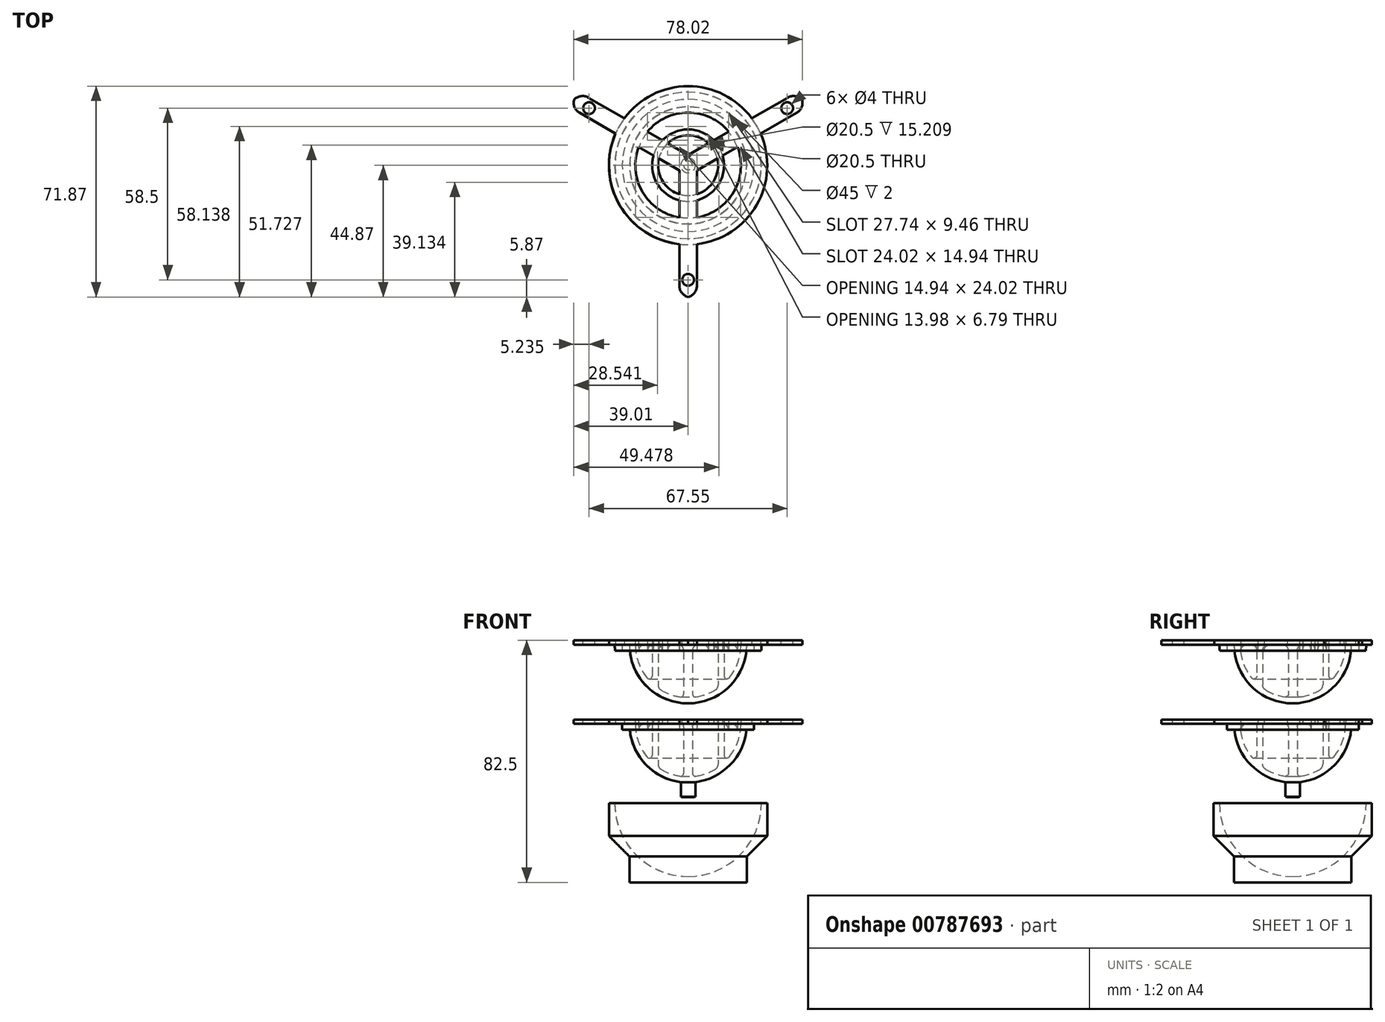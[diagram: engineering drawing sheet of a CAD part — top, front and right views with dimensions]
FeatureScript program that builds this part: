
annotation { "Feature Type Name" : "Feature", "Feature Type Description" : "" }
export const myFeature = defineFeature(function(context is Context, id is Id, definition is map)
    precondition{}
    {
        {
            var Q0;
            Q0=qCreatedBy(makeId("Front.planeOp"),FACE);
            var sketch = newSketch(context, id + "F0", { "sketchPlane" : qUnion([Q0])});
            skLineSegment(sketch, "E0.bottom", {"start": v(0, 0) * mm, "end": v(-27, 0) * mm});
            skLineSegment(sketch, "E0.top", {"start": v(0, 27) * mm, "end": v(-27, 27) * mm});
            skLineSegment(sketch, "E0.left", {"start": v(0, 0) * mm, "end": v(0, 27) * mm});
            skLineSegment(sketch, "E0.right", {"start": v(-27, 0) * mm, "end": v(-27, 27) * mm});
            skArc(sketch, "E1", {"start": v(-25, 27) * mm, "mid": v(-17.68, 9.32) * mm, "end": v(0, 2) * mm});
            skLineSegment(sketch, "E2", {"start": v(-25, 27) * mm, "end": v(-25, 19.7) * mm, "construction": true});
            skLineSegment(sketch, "E3", {"start": v(0, 2) * mm, "end": v(-8.55, 2) * mm, "construction": true});
            skArc(sketch, "E4", {"start": v(-20, 27) * mm, "mid": v(-14.14, 12.86) * mm, "end": v(0, 7) * mm});
            skLineSegment(sketch, "E5", {"start": v(-20, 27) * mm, "end": v(-20, 19.7) * mm, "construction": true});
            skLineSegment(sketch, "E6", {"start": v(0, 7) * mm, "end": v(-8.55, 7) * mm, "construction": true});
            skLineSegment(sketch, "E7", {"start": v(-27, 15.82) * mm, "end": v(-11.18, 0) * mm});
            skPoint(sketch, "E8", {"position": v(-13.5, 0) * mm});
            skLineSegment(sketch, "E9.bottom", {"start": v(0, 27) * mm, "end": v(-22.5, 27) * mm});
            skLineSegment(sketch, "E9.top", {"start": v(0, 25) * mm, "end": v(-22.5, 25) * mm});
            skLineSegment(sketch, "E9.left", {"start": v(0, 27) * mm, "end": v(0, 25) * mm});
            skLineSegment(sketch, "E9.right", {"start": v(-22.5, 27) * mm, "end": v(-22.5, 25) * mm});
            skLineSegment(sketch, "E10", {"start": v(-30, 0) * mm, "end": v(-30, 18.82) * mm});
            skLineSegment(sketch, "E11.top", {"start": v(0, 28.5) * mm, "end": v(-27, 28.5) * mm});
            skLineSegment(sketch, "E11.left", {"start": v(0, 27) * mm, "end": v(0, 28.5) * mm});
            skLineSegment(sketch, "E11.right", {"start": v(-27, 27) * mm, "end": v(-27, 28.5) * mm});
            skLineSegment(sketch, "E12.bottom", {"start": v(-3, 28.5) * mm, "end": v(3, 28.5) * mm});
            skLineSegment(sketch, "E12.top", {"start": v(-3, 27) * mm, "end": v(3, 27) * mm});
            skLineSegment(sketch, "E12.left", {"start": v(-3, 28.5) * mm, "end": v(-3, 27) * mm});
            skLineSegment(sketch, "E12.right", {"start": v(3, 28.5) * mm, "end": v(3, 27) * mm});
            skArc(sketch, "E13", {"start": v(-18, 27) * mm, "mid": v(-16.98, 21.02) * mm, "end": v(-14.03, 15.72) * mm, "construction": true});
            skLineSegment(sketch, "E14.bottom", {"start": v(0, 25) * mm, "end": v(-1.5, 25) * mm});
            skLineSegment(sketch, "E14.left", {"start": v(0, 25) * mm, "end": v(0, 7) * mm});
            skLineSegment(sketch, "E14.right", {"start": v(-1.5, 25) * mm, "end": v(-1.5, 10.18) * mm});
            skArc(sketch, "E15.filletArc", {"start": v(-2.65, 9.2) * mm, "mid": v(-1.85, 9.43) * mm, "end": v(-1.5, 10.18) * mm});
            skLineSegment(sketch, "E16", {"start": v(-11.25, 25) * mm, "end": v(-11.25, 12.95) * mm, "construction": true});
            skLineSegment(sketch, "E17", {"start": v(-12.25, 25) * mm, "end": v(-12.25, 16.35) * mm});
            skLineSegment(sketch, "E18", {"start": v(-10.25, 25) * mm, "end": v(-10.25, 13.3) * mm});
            skArc(sketch, "E19", {"start": v(-18, 27) * mm, "mid": v(-16.98, 21.02) * mm, "end": v(-14.03, 15.72) * mm});
            skArc(sketch, "E20", {"start": v(-9.28, 11.58) * mm, "mid": v(-6.08, 10.06) * mm, "end": v(-2.65, 9.2) * mm});
            skArc(sketch, "E21.filletArc", {"start": v(-14.03, 15.72) * mm, "mid": v(-12.92, 15.4) * mm, "end": v(-12.25, 16.35) * mm});
            skPoint(sketch, "E22.visualSharp", {"position": v(-10.25, 12.2) * mm});
            skArc(sketch, "E22.filletArc", {"start": v(-10.25, 13.3) * mm, "mid": v(-10, 12.3) * mm, "end": v(-9.28, 11.58) * mm});
            skLineSegment(sketch, "E23", {"start": v(-12.25, 25) * mm, "end": v(-12.25, 28.5) * mm});
            skLineSegment(sketch, "E24", {"start": v(-10.25, 25) * mm, "end": v(-10.25, 28.5) * mm});
            skLineSegment(sketch, "E25", {"start": v(-18, 27) * mm, "end": v(-18, 28.5) * mm});
            skLineSegment(sketch, "E26", {"start": v(-1.5, 25) * mm, "end": v(-1.5, 27) * mm});
            skLineSegment(sketch, "E27", {"start": v(-2.5, 7.16) * mm, "end": v(-2.5, 2.13) * mm});
            skLineSegment(sketch, "E28", {"start": v(-22.5, 25) * mm, "end": v(-24.92, 25) * mm});
            skLineSegment(sketch, "E29", {"start": v(-20, 0) * mm, "end": v(-20, 8.82) * mm});
            skSolve(sketch);
        }
        {
            var Q0;
            {var subQ0=sQuery(id+"F0.wireOp",EDGE,"E0.left");var subQ1=sQuery(id+"F0.wireOp",EDGE,"E0.bottom");var subQ2=makeQuery(id+"F0.imprint","INTERSECT",VERTEX,{"derivedFrom":[subQ1,subQ0]});Q0=makeQuery(id+"F0.imprint","IMPRINT",FACE,{"disambiguationData":[TD([[makeQuery(id+"F0.imprint","IMPRINT",EDGE,{"disambiguationData":[TD([[subQ2,-1.0]])],"derivedFrom":subQ1}),-1.0]])]});}
            var Q1;
            {var subQ3=sQuery(id+"F0.wireOp",EDGE,"E10");Q1=makeQuery(id+"F0.imprint","IMPRINT",FACE,{"disambiguationData":[TD([[makeQuery(id+"F0.imprint","IMPRINT",EDGE,{"derivedFrom":subQ3}),-1.0]])]});}
            var Q2;
            {var subQ0=sQuery(id+"F0.wireOp",EDGE,"E29");Q2=makeQuery(id+"F0.imprint","IMPRINT",FACE,{"disambiguationData":[TD([[makeQuery(id+"F0.imprint","IMPRINT",EDGE,{"derivedFrom":subQ0}),-1.0]])]});}
            var Q3;
            Q3=sQuery(id+"F0.wireOp",EDGE,"E0.left");
            revolve(context, id + "F1", {"surfaceOperationType" : NewSurfaceOperationType.NEW, "entities" : qUnion([Q0, Q1, Q2]), "axis" : qUnion([Q3]), "revolveType" : RevolveType.FULL});
        }
        {
            var Q0;
            {var subQ6=sQuery(id+"F0.wireOp",EDGE,"E14.right");Q0=makeQuery(id+"F0.imprint","IMPRINT",FACE,{"disambiguationData":[TD([[makeQuery(id+"F0.imprint","IMPRINT",EDGE,{"derivedFrom":subQ6}),1.0]])]});}
            var Q1;
            {var subQ5=sQuery(id+"F0.wireOp",EDGE,"E27");Q1=makeQuery(id+"F0.imprint","IMPRINT",FACE,{"disambiguationData":[TD([[makeQuery(id+"F0.imprint","IMPRINT",EDGE,{"derivedFrom":subQ5}),1.0]])]});}
            var Q2;
            {var subQ0=sQuery(id+"F0.wireOp",EDGE,"E26");Q2=makeQuery(id+"F0.imprint","IMPRINT",FACE,{"disambiguationData":[TD([[makeQuery(id+"F0.imprint","IMPRINT",EDGE,{"derivedFrom":subQ0}),-1.0]])]});}
            var Q3;
            {var subQ0=sQuery(id+"F0.wireOp",EDGE,"E11.left");Q3=makeQuery(id+"F0.imprint","IMPRINT",FACE,{"disambiguationData":[TD([[makeQuery(id+"F0.imprint","IMPRINT",EDGE,{"derivedFrom":subQ0}),1.0]])]});}
            var Q4;
            {var subQ0=sQuery(id+"F0.wireOp",EDGE,"E24");var subQ1=sQuery(id+"F0.wireOp",EDGE,"E0.top");var subQ2=makeQuery(id+"F0.imprint","INTERSECT",VERTEX,{"derivedFrom":[subQ1,subQ0]});Q4=makeQuery(id+"F0.imprint","IMPRINT",FACE,{"disambiguationData":[TD([[makeQuery(id+"F0.imprint","IMPRINT",EDGE,{"disambiguationData":[TD([[subQ2,-1.0]])],"derivedFrom":subQ1}),1.0]])]});}
            var Q5;
            {var subQ0=sQuery(id+"F0.wireOp",EDGE,"E24");var subQ1=sQuery(id+"F0.wireOp",EDGE,"E0.top");var subQ2=makeQuery(id+"F0.imprint","INTERSECT",VERTEX,{"derivedFrom":[subQ1,subQ0]});Q5=makeQuery(id+"F0.imprint","IMPRINT",FACE,{"disambiguationData":[TD([[makeQuery(id+"F0.imprint","IMPRINT",EDGE,{"disambiguationData":[TD([[subQ2,-1.0]])],"derivedFrom":subQ1}),-1.0]])]});}
            var Q6;
            {var subQ0=sQuery(id+"F0.wireOp",EDGE,"E4");var subQ1=sQuery(id+"F0.wireOp",EDGE,"E0.top");var subQ2=makeQuery(id+"F0.imprint","INTERSECT",VERTEX,{"derivedFrom":[subQ1,subQ0]});Q6=makeQuery(id+"F0.imprint","IMPRINT",FACE,{"disambiguationData":[TD([[makeQuery(id+"F0.imprint","IMPRINT",EDGE,{"disambiguationData":[TD([[subQ2,-1.0]])],"derivedFrom":subQ0}),1.0]])]});}
            var Q7;
            {var subQ3=sQuery(id+"F0.wireOp",EDGE,"E9.right");Q7=makeQuery(id+"F0.imprint","IMPRINT",FACE,{"disambiguationData":[TD([[makeQuery(id+"F0.imprint","IMPRINT",EDGE,{"derivedFrom":subQ3}),1.0]])]});}
            var Q8;
            {var subQ3=sQuery(id+"F0.wireOp",EDGE,"E11.right");Q8=makeQuery(id+"F0.imprint","IMPRINT",FACE,{"disambiguationData":[TD([[makeQuery(id+"F0.imprint","IMPRINT",EDGE,{"derivedFrom":subQ3}),-1.0]])]});}
            var Q9;
            Q9=sQuery(id+"F0.wireOp",EDGE,"E0.left");
            revolve(context, id + "F2", {"surfaceOperationType" : NewSurfaceOperationType.NEW, "entities" : qUnion([Q0, Q1, Q2, Q3, Q4, Q5, Q6, Q7, Q8]), "axis" : qUnion([Q9]), "revolveType" : RevolveType.FULL});
        }
        {
            var Q0;
            {var subQ6=sQuery(id+"F0.wireOp",EDGE,"E14.right");Q0=makeQuery(id+"F0.imprint","IMPRINT",FACE,{"disambiguationData":[TD([[makeQuery(id+"F0.imprint","IMPRINT",EDGE,{"derivedFrom":subQ6}),1.0]])]});}
            var Q1;
            {var subQ0=sQuery(id+"F0.wireOp",EDGE,"E26");Q1=makeQuery(id+"F0.imprint","IMPRINT",FACE,{"disambiguationData":[TD([[makeQuery(id+"F0.imprint","IMPRINT",EDGE,{"derivedFrom":subQ0}),-1.0]])]});}
            var Q2;
            {var subQ0=sQuery(id+"F0.wireOp",EDGE,"E11.left");Q2=makeQuery(id+"F0.imprint","IMPRINT",FACE,{"disambiguationData":[TD([[makeQuery(id+"F0.imprint","IMPRINT",EDGE,{"derivedFrom":subQ0}),1.0]])]});}
            var Q3;
            {var subQ0=sQuery(id+"F0.wireOp",EDGE,"E24");var subQ1=sQuery(id+"F0.wireOp",EDGE,"E0.top");var subQ2=makeQuery(id+"F0.imprint","INTERSECT",VERTEX,{"derivedFrom":[subQ1,subQ0]});Q3=makeQuery(id+"F0.imprint","IMPRINT",FACE,{"disambiguationData":[TD([[makeQuery(id+"F0.imprint","IMPRINT",EDGE,{"disambiguationData":[TD([[subQ2,-1.0]])],"derivedFrom":subQ1}),1.0]])]});}
            var Q4;
            {var subQ0=sQuery(id+"F0.wireOp",EDGE,"E24");var subQ1=sQuery(id+"F0.wireOp",EDGE,"E0.top");var subQ2=makeQuery(id+"F0.imprint","INTERSECT",VERTEX,{"derivedFrom":[subQ1,subQ0]});Q4=makeQuery(id+"F0.imprint","IMPRINT",FACE,{"disambiguationData":[TD([[makeQuery(id+"F0.imprint","IMPRINT",EDGE,{"disambiguationData":[TD([[subQ2,-1.0]])],"derivedFrom":subQ1}),-1.0]])]});}
            var Q5;
            {var subQ0=sQuery(id+"F0.wireOp",EDGE,"E4");var subQ1=sQuery(id+"F0.wireOp",EDGE,"E0.top");var subQ2=makeQuery(id+"F0.imprint","INTERSECT",VERTEX,{"derivedFrom":[subQ1,subQ0]});Q5=makeQuery(id+"F0.imprint","IMPRINT",FACE,{"disambiguationData":[TD([[makeQuery(id+"F0.imprint","IMPRINT",EDGE,{"disambiguationData":[TD([[subQ2,-1.0]])],"derivedFrom":subQ0}),1.0]])]});}
            var Q6;
            {var subQ3=sQuery(id+"F0.wireOp",EDGE,"E11.right");Q6=makeQuery(id+"F0.imprint","IMPRINT",FACE,{"disambiguationData":[TD([[makeQuery(id+"F0.imprint","IMPRINT",EDGE,{"derivedFrom":subQ3}),-1.0]])]});}
            var Q7;
            {var subQ3=sQuery(id+"F0.wireOp",EDGE,"E9.right");Q7=makeQuery(id+"F0.imprint","IMPRINT",FACE,{"disambiguationData":[TD([[makeQuery(id+"F0.imprint","IMPRINT",EDGE,{"derivedFrom":subQ3}),-1.0]])]});}
            var Q8;
            Q8=sQuery(id+"F0.wireOp",EDGE,"E0.left");
            revolve(context, id + "F3", {"surfaceOperationType" : NewSurfaceOperationType.NEW, "entities" : qUnion([Q0, Q1, Q2, Q3, Q4, Q5, Q6, Q7]), "axis" : qUnion([Q8]), "revolveType" : RevolveType.FULL});
        }
        {
            var Q0;
            Q0=makeQuery(id+"F2.opRevolve","SWEPT_EDGE",EDGE,{"disambiguationData":[OSD([sQuery(id+"F0.wireOp",EDGE,"E0.top"),sQuery(id+"F0.wireOp",EDGE,"E26")])]});
            fillet(context, id + "F4", {"entities" : qUnion([Q0]), "radius" : 1 * mm, "tangentPropagation" : true, "allowEdgeOverflow" : false});
        }
        {
            var Q0;
            Q0=makeQuery(id+"F0.imprint","IMPRINT",FACE,{"disambiguationData":[TD([[makeQuery(id+"F0.imprint","IMPRINT",EDGE,{"derivedFrom":sQuery(id+"F0.wireOp",EDGE,"E11.left")}),-1.0]])]});
            var Q1;
            {var subQ0=sQuery(id+"F0.wireOp",EDGE,"E11.left");Q1=makeQuery(id+"F0.imprint","IMPRINT",FACE,{"disambiguationData":[TD([[makeQuery(id+"F0.imprint","IMPRINT",EDGE,{"derivedFrom":subQ0}),1.0]])]});}
            extrude(context, id + "F5", {"entities" : qUnion([Q0, Q1]), "depth" : 45 * mm, "offsetDistance" : 25 * mm});
        }
        {
            var Q0;
            Q0=makeQuery(id+"F5.opExtrude","SWEPT_FACE",FACE,{"disambiguationData":[OSD([sQuery(id+"F0.wireOp",EDGE,"E11.top"),sQuery(id+"F0.wireOp",EDGE,"E12.bottom")])]});
            var sketch = newSketch(context, id + "F6", { "sketchPlane" : qUnion([Q0])});
            skLineSegment(sketch, "E30.0", {"start": v(-3, -45) * mm, "end": v(-3, 0) * mm});
            skLineSegment(sketch, "E30.1", {"start": v(-3, -45) * mm, "end": v(3, -45) * mm});
            skLineSegment(sketch, "E30.2", {"start": v(3, -45) * mm, "end": v(3, 0) * mm});
            skLineSegment(sketch, "E31", {"start": v(0, -65.08) * mm, "end": v(0, -45) * mm, "construction": true});
            skLineSegment(sketch, "E32", {"start": v(3, -39) * mm, "end": v(-3, -39) * mm, "construction": true});
            skCircle(sketch, "E33", {"center": v(0, -39) * mm, "radius": 2 * mm});
            skSolve(sketch);
        }
        {
            var Q0;
            Q0=makeQuery(id+"F6.imprint","IMPRINT",FACE,{"disambiguationData":[TD([[makeQuery(id+"F6.imprint","IMPRINT",EDGE,{"derivedFrom":sQuery(id+"F6.wireOp",EDGE,"E33")}),1.0]])]});
            extrude(context, id + "F7", {"entities" : qUnion([Q0]), "operationType" : NewBodyOperationType.REMOVE, "endBound" : BoundingType.UP_TO_NEXT, "oppositeDirection" : true, "depth" : 25 * mm, "offsetDistance" : 25 * mm});
        }
        {
            var Q0;
            Q0=makeQuery(id+"F5.opExtrude","CAP_EDGE",EDGE,{"disambiguationData":[OSD([sQuery(id+"F0.wireOp",EDGE,"E12.right")])],"isStart":false});
            var Q1;
            Q1=makeQuery(id+"F5.opExtrude","CAP_EDGE",EDGE,{"disambiguationData":[OSD([sQuery(id+"F0.wireOp",EDGE,"E12.left")])],"isStart":false});
            fillet(context, id + "F8", {"entities" : qUnion([Q0, Q1]), "radius" : 4 * mm, "tangentPropagation" : true, "allowEdgeOverflow" : false});
        }
        {
            var Q0;
            Q0=makeQuery(id+"F5.opExtrude","SWEPT_BODY",BODY,{"disambiguationData":[OSD([sQuery(id+"F0.wireOp",EDGE,"E0.top"),sQuery(id+"F0.wireOp",EDGE,"E11.top"),sQuery(id+"F0.wireOp",EDGE,"E12.bottom"),sQuery(id+"F0.wireOp",EDGE,"E12.top"),sQuery(id+"F0.wireOp",EDGE,"E12.left"),sQuery(id+"F0.wireOp",EDGE,"E12.right")])]});
            var Q1;
            Q1=sQuery(id+"F0.wireOp",EDGE,"E0.left");
            circularPattern(context, id + "F9", {"entities" : qUnion([Q0]), "axis" : qUnion([Q1]), "angle" : 360 * degree, "instanceCount" : 3, "equalSpace" : true});
        }
        {
            var Q0;
            Q0=makeQuery(id+"F5.opExtrude","SWEPT_BODY",BODY,{"disambiguationData":[OSD([sQuery(id+"F0.wireOp",EDGE,"E0.top"),sQuery(id+"F0.wireOp",EDGE,"E11.top"),sQuery(id+"F0.wireOp",EDGE,"E12.bottom"),sQuery(id+"F0.wireOp",EDGE,"E12.top"),sQuery(id+"F0.wireOp",EDGE,"E12.left"),sQuery(id+"F0.wireOp",EDGE,"E12.right")])]});
            var Q1;
            Q1=makeQuery(id+"F9.opPattern","COPY",BODY,{"derivedFrom":makeQuery(id+"F5.opExtrude","SWEPT_BODY",BODY,{"disambiguationData":[OSD([sQuery(id+"F0.wireOp",EDGE,"E0.top"),sQuery(id+"F0.wireOp",EDGE,"E11.top"),sQuery(id+"F0.wireOp",EDGE,"E12.bottom"),sQuery(id+"F0.wireOp",EDGE,"E12.top"),sQuery(id+"F0.wireOp",EDGE,"E12.left"),sQuery(id+"F0.wireOp",EDGE,"E12.right")])]}),"instanceName":"2"});
            var Q2;
            Q2=makeQuery(id+"F9.opPattern","COPY",BODY,{"derivedFrom":makeQuery(id+"F5.opExtrude","SWEPT_BODY",BODY,{"disambiguationData":[OSD([sQuery(id+"F0.wireOp",EDGE,"E0.top"),sQuery(id+"F0.wireOp",EDGE,"E11.top"),sQuery(id+"F0.wireOp",EDGE,"E12.bottom"),sQuery(id+"F0.wireOp",EDGE,"E12.top"),sQuery(id+"F0.wireOp",EDGE,"E12.left"),sQuery(id+"F0.wireOp",EDGE,"E12.right")])]}),"instanceName":"1"});
            booleanBodies(context, id + "F10", {"operationType" : BooleanOperationType.UNION, "tools" : qUnion([Q0, Q1, Q2])});
        }
        {
            var Q0;
            Q0=makeQuery(id+"F5.opExtrude","SWEPT_BODY",BODY,{"disambiguationData":[OSD([sQuery(id+"F0.wireOp",EDGE,"E0.top"),sQuery(id+"F0.wireOp",EDGE,"E11.top"),sQuery(id+"F0.wireOp",EDGE,"E12.bottom"),sQuery(id+"F0.wireOp",EDGE,"E12.top"),sQuery(id+"F0.wireOp",EDGE,"E12.left"),sQuery(id+"F0.wireOp",EDGE,"E12.right")])]});
            transform(context, id + "F11", {"entities" : qUnion([Q0]), "transformType" : TransformType.TRANSLATION_3D, "dx" : 0 * mm, "dy" : 0 * mm, "dz" : 0 * mm, "makeCopy" : true});
        }
        {
            var Q0;
            Q0=makeQuery(id+"F2.opRevolve","SWEPT_BODY",BODY,{"disambiguationData":[OSD([sQuery(id+"F0.wireOp",EDGE,"E0.top"),sQuery(id+"F0.wireOp",EDGE,"E0.left"),sQuery(id+"F0.wireOp",EDGE,"E1"),sQuery(id+"F0.wireOp",EDGE,"E4"),sQuery(id+"F0.wireOp",EDGE,"E9.top"),sQuery(id+"F0.wireOp",EDGE,"E9.right"),sQuery(id+"F0.wireOp",EDGE,"E11.top"),sQuery(id+"F0.wireOp",EDGE,"E11.left"),sQuery(id+"F0.wireOp",EDGE,"E11.right"),sQuery(id+"F0.wireOp",EDGE,"E12.left"),sQuery(id+"F0.wireOp",EDGE,"E14.right"),sQuery(id+"F0.wireOp",EDGE,"E15.filletArc"),sQuery(id+"F0.wireOp",EDGE,"E17"),sQuery(id+"F0.wireOp",EDGE,"E18"),sQuery(id+"F0.wireOp",EDGE,"E19"),sQuery(id+"F0.wireOp",EDGE,"E20"),sQuery(id+"F0.wireOp",EDGE,"E21.filletArc"),sQuery(id+"F0.wireOp",EDGE,"E22.filletArc"),sQuery(id+"F0.wireOp",EDGE,"E23"),sQuery(id+"F0.wireOp",EDGE,"E24"),sQuery(id+"F0.wireOp",EDGE,"E25"),sQuery(id+"F0.wireOp",EDGE,"E26"),sQuery(id+"F0.wireOp",EDGE,"E27")])]});
            var Q1;
            Q1=makeQuery(id+"F5.opExtrude","SWEPT_BODY",BODY,{"disambiguationData":[OSD([sQuery(id+"F0.wireOp",EDGE,"E0.top"),sQuery(id+"F0.wireOp",EDGE,"E11.top"),sQuery(id+"F0.wireOp",EDGE,"E12.bottom"),sQuery(id+"F0.wireOp",EDGE,"E12.top"),sQuery(id+"F0.wireOp",EDGE,"E12.left"),sQuery(id+"F0.wireOp",EDGE,"E12.right")])]});
            booleanBodies(context, id + "F12", {"operationType" : BooleanOperationType.UNION, "tools" : qUnion([Q0, Q1])});
        }
        {
            var Q0;
            Q0=makeQuery(id+"F10.opBoolean","INTERSECT",EDGE,{"disambiguationData":[OD(0.0)],"derivedFrom":[makeQuery(id+"F2.opRevolve","SWEPT_FACE",FACE,{"disambiguationData":[OSD([sQuery(id+"F0.wireOp",EDGE,"E18"),sQuery(id+"F0.wireOp",EDGE,"E24")])]}),makeQuery(id+"F9.opPattern","COPY",FACE,{"derivedFrom":makeQuery(id+"F5.opExtrude","SWEPT_FACE",FACE,{"disambiguationData":[OSD([sQuery(id+"F0.wireOp",EDGE,"E12.top")])]}),"instanceName":"1"})]});
            var Q1;
            Q1=makeQuery(id+"F10.opBoolean","INTERSECT",EDGE,{"disambiguationData":[OD(0.0)],"derivedFrom":[makeQuery(id+"F2.opRevolve","SWEPT_FACE",FACE,{"disambiguationData":[OSD([sQuery(id+"F0.wireOp",EDGE,"E17"),sQuery(id+"F0.wireOp",EDGE,"E23")])]}),makeQuery(id+"F9.opPattern","COPY",FACE,{"derivedFrom":makeQuery(id+"F5.opExtrude","SWEPT_FACE",FACE,{"disambiguationData":[OSD([sQuery(id+"F0.wireOp",EDGE,"E12.top")])]}),"instanceName":"1"})]});
            var Q2;
            {var subQ0=sQuery(id+"F0.wireOp",EDGE,"E25");var subQ1=makeQuery(id+"F2.opRevolve","SWEPT_FACE",FACE,{"disambiguationData":[OSD([subQ0])]});var subQ2=sQuery(id+"F0.wireOp",EDGE,"E0.top");var subQ3=makeQuery(id+"F5.opExtrude","SWEPT_FACE",FACE,{"disambiguationData":[OSD([subQ2,sQuery(id+"F0.wireOp",EDGE,"E12.top")])]});var subQ4=subQ3;var subQ5=makeQuery(id+"F9.opPattern","COPY",FACE,{"derivedFrom":subQ4,"instanceName":"1"});var subQ6=sQuery(id+"F0.wireOp",EDGE,"E19");var subQ7=makeQuery(id+"F2.opRevolve","SWEPT_FACE",FACE,{"disambiguationData":[OSD([subQ6])]});var subQ8=makeQuery(id+"F5.opExtrude","SWEPT_FACE",FACE,{"disambiguationData":[OSD([sQuery(id+"F0.wireOp",EDGE,"E12.left")])]});var subQ9=subQ8;var subQ10=makeQuery(id+"F9.opPattern","COPY",FACE,{"derivedFrom":subQ9,"instanceName":"2"});var subQ11=makeQuery(id+"F5.opExtrude","SWEPT_FACE",FACE,{"disambiguationData":[OSD([sQuery(id+"F0.wireOp",EDGE,"E12.right")])]});var subQ12=subQ11;var subQ14=makeQuery(id+"F9.opPattern","COPY",FACE,{"derivedFrom":subQ4,"instanceName":"2"});var subQ15=makeQuery(id+"F2.opRevolve","SWEPT_EDGE",EDGE,{"disambiguationData":[OSD([subQ2,subQ6,subQ0])]});var subQ16=makeQuery(id+"F9.opPattern","COPY",FACE,{"derivedFrom":subQ9,"instanceName":"1"});var subQ17=makeQuery(id+"F9.opPattern","COPY",FACE,{"derivedFrom":subQ12,"instanceName":"1"});Q2=qUnion([makeQuery(id+"F12.opBoolean","SPLIT",EDGE,{"disambiguationData":[topologyDisambiguationEdgeConnected([subQ7,subQ1]),TD([subQ17])],"derivedFrom":subQ15}),makeQuery(id+"F12.opBoolean","SPLIT",EDGE,{"disambiguationData":[topologyDisambiguationEdgeConnected([subQ7,subQ3,subQ5,subQ14]),TD([subQ8])],"derivedFrom":subQ15}),makeQuery(id+"F12.opBoolean","SPLIT",EDGE,{"disambiguationData":[topologyDisambiguationEdgeConnected([subQ7,subQ3,subQ5,subQ14]),TD([subQ16])],"derivedFrom":subQ15}),makeQuery(id+"F12.opBoolean","SPLIT",EDGE,{"disambiguationData":[topologyDisambiguationEdgeConnected([subQ7,subQ1]),TD([subQ11])],"derivedFrom":subQ15}),makeQuery(id+"F12.opBoolean","SPLIT",EDGE,{"disambiguationData":[topologyDisambiguationEdgeConnected([subQ7,subQ1]),TD([subQ8])],"derivedFrom":subQ15}),makeQuery(id+"F12.opBoolean","SPLIT",EDGE,{"disambiguationData":[topologyDisambiguationEdgeConnected([subQ7,subQ3,subQ5,subQ14]),TD([subQ10])],"derivedFrom":subQ15})]);}
            var Q3;
            Q3=makeQuery(id+"F10.opBoolean","INTERSECT",EDGE,{"disambiguationData":[OD(2.0)],"derivedFrom":[makeQuery(id+"F2.opRevolve","SWEPT_FACE",FACE,{"disambiguationData":[OSD([sQuery(id+"F0.wireOp",EDGE,"E18"),sQuery(id+"F0.wireOp",EDGE,"E24")])]}),makeQuery(id+"F9.opPattern","COPY",FACE,{"derivedFrom":makeQuery(id+"F5.opExtrude","SWEPT_FACE",FACE,{"disambiguationData":[OSD([sQuery(id+"F0.wireOp",EDGE,"E12.top")])]}),"instanceName":"1"})]});
            var Q4;
            Q4=makeQuery(id+"F10.opBoolean","INTERSECT",EDGE,{"disambiguationData":[OD(2.0)],"derivedFrom":[makeQuery(id+"F2.opRevolve","SWEPT_FACE",FACE,{"disambiguationData":[OSD([sQuery(id+"F0.wireOp",EDGE,"E17"),sQuery(id+"F0.wireOp",EDGE,"E23")])]}),makeQuery(id+"F9.opPattern","COPY",FACE,{"derivedFrom":makeQuery(id+"F5.opExtrude","SWEPT_FACE",FACE,{"disambiguationData":[OSD([sQuery(id+"F0.wireOp",EDGE,"E12.top")])]}),"instanceName":"1"})]});
            var Q5;
            {var subQ0=sQuery(id+"F0.wireOp",EDGE,"E25");var subQ1=makeQuery(id+"F2.opRevolve","SWEPT_FACE",FACE,{"disambiguationData":[OSD([subQ0])]});var subQ2=sQuery(id+"F0.wireOp",EDGE,"E0.top");var subQ3=makeQuery(id+"F5.opExtrude","SWEPT_FACE",FACE,{"disambiguationData":[OSD([subQ2,sQuery(id+"F0.wireOp",EDGE,"E12.top")])]});var subQ4=subQ3;var subQ5=makeQuery(id+"F9.opPattern","COPY",FACE,{"derivedFrom":subQ4,"instanceName":"1"});var subQ6=sQuery(id+"F0.wireOp",EDGE,"E19");var subQ7=makeQuery(id+"F2.opRevolve","SWEPT_FACE",FACE,{"disambiguationData":[OSD([subQ6])]});var subQ8=makeQuery(id+"F5.opExtrude","SWEPT_FACE",FACE,{"disambiguationData":[OSD([sQuery(id+"F0.wireOp",EDGE,"E12.left")])]});var subQ9=subQ8;var subQ10=makeQuery(id+"F9.opPattern","COPY",FACE,{"derivedFrom":subQ9,"instanceName":"2"});var subQ11=makeQuery(id+"F5.opExtrude","SWEPT_FACE",FACE,{"disambiguationData":[OSD([sQuery(id+"F0.wireOp",EDGE,"E12.right")])]});var subQ12=subQ11;var subQ14=makeQuery(id+"F9.opPattern","COPY",FACE,{"derivedFrom":subQ4,"instanceName":"2"});var subQ15=makeQuery(id+"F2.opRevolve","SWEPT_EDGE",EDGE,{"disambiguationData":[OSD([subQ2,subQ6,subQ0])]});var subQ16=makeQuery(id+"F9.opPattern","COPY",FACE,{"derivedFrom":subQ9,"instanceName":"1"});var subQ17=makeQuery(id+"F9.opPattern","COPY",FACE,{"derivedFrom":subQ12,"instanceName":"1"});Q5=qUnion([makeQuery(id+"F12.opBoolean","SPLIT",EDGE,{"disambiguationData":[topologyDisambiguationEdgeConnected([subQ7,subQ1]),TD([subQ17])],"derivedFrom":subQ15}),makeQuery(id+"F12.opBoolean","SPLIT",EDGE,{"disambiguationData":[topologyDisambiguationEdgeConnected([subQ7,subQ3,subQ5,subQ14]),TD([subQ8])],"derivedFrom":subQ15}),makeQuery(id+"F12.opBoolean","SPLIT",EDGE,{"disambiguationData":[topologyDisambiguationEdgeConnected([subQ7,subQ3,subQ5,subQ14]),TD([subQ16])],"derivedFrom":subQ15}),makeQuery(id+"F12.opBoolean","SPLIT",EDGE,{"disambiguationData":[topologyDisambiguationEdgeConnected([subQ7,subQ1]),TD([subQ11])],"derivedFrom":subQ15}),makeQuery(id+"F12.opBoolean","SPLIT",EDGE,{"disambiguationData":[topologyDisambiguationEdgeConnected([subQ7,subQ1]),TD([subQ8])],"derivedFrom":subQ15}),makeQuery(id+"F12.opBoolean","SPLIT",EDGE,{"disambiguationData":[topologyDisambiguationEdgeConnected([subQ7,subQ3,subQ5,subQ14]),TD([subQ10])],"derivedFrom":subQ15})]);}
            var Q6;
            Q6=makeQuery(id+"F10.opBoolean","INTERSECT",EDGE,{"disambiguationData":[OD(1.0)],"derivedFrom":[makeQuery(id+"F2.opRevolve","SWEPT_FACE",FACE,{"disambiguationData":[OSD([sQuery(id+"F0.wireOp",EDGE,"E18"),sQuery(id+"F0.wireOp",EDGE,"E24")])]}),makeQuery(id+"F9.opPattern","COPY",FACE,{"derivedFrom":makeQuery(id+"F5.opExtrude","SWEPT_FACE",FACE,{"disambiguationData":[OSD([sQuery(id+"F0.wireOp",EDGE,"E12.top")])]}),"instanceName":"1"})]});
            var Q7;
            Q7=makeQuery(id+"F10.opBoolean","INTERSECT",EDGE,{"disambiguationData":[OD(1.0)],"derivedFrom":[makeQuery(id+"F2.opRevolve","SWEPT_FACE",FACE,{"disambiguationData":[OSD([sQuery(id+"F0.wireOp",EDGE,"E17"),sQuery(id+"F0.wireOp",EDGE,"E23")])]}),makeQuery(id+"F9.opPattern","COPY",FACE,{"derivedFrom":makeQuery(id+"F5.opExtrude","SWEPT_FACE",FACE,{"disambiguationData":[OSD([sQuery(id+"F0.wireOp",EDGE,"E12.top")])]}),"instanceName":"1"})]});
            var Q8;
            {var subQ0=sQuery(id+"F0.wireOp",EDGE,"E25");var subQ1=makeQuery(id+"F2.opRevolve","SWEPT_FACE",FACE,{"disambiguationData":[OSD([subQ0])]});var subQ2=sQuery(id+"F0.wireOp",EDGE,"E0.top");var subQ3=makeQuery(id+"F5.opExtrude","SWEPT_FACE",FACE,{"disambiguationData":[OSD([subQ2,sQuery(id+"F0.wireOp",EDGE,"E12.top")])]});var subQ4=subQ3;var subQ5=makeQuery(id+"F9.opPattern","COPY",FACE,{"derivedFrom":subQ4,"instanceName":"1"});var subQ6=sQuery(id+"F0.wireOp",EDGE,"E19");var subQ7=makeQuery(id+"F2.opRevolve","SWEPT_FACE",FACE,{"disambiguationData":[OSD([subQ6])]});var subQ8=makeQuery(id+"F5.opExtrude","SWEPT_FACE",FACE,{"disambiguationData":[OSD([sQuery(id+"F0.wireOp",EDGE,"E12.left")])]});var subQ9=subQ8;var subQ10=makeQuery(id+"F9.opPattern","COPY",FACE,{"derivedFrom":subQ9,"instanceName":"2"});var subQ11=makeQuery(id+"F5.opExtrude","SWEPT_FACE",FACE,{"disambiguationData":[OSD([sQuery(id+"F0.wireOp",EDGE,"E12.right")])]});var subQ12=subQ11;var subQ14=makeQuery(id+"F9.opPattern","COPY",FACE,{"derivedFrom":subQ4,"instanceName":"2"});var subQ15=makeQuery(id+"F2.opRevolve","SWEPT_EDGE",EDGE,{"disambiguationData":[OSD([subQ2,subQ6,subQ0])]});var subQ16=makeQuery(id+"F9.opPattern","COPY",FACE,{"derivedFrom":subQ9,"instanceName":"1"});var subQ17=makeQuery(id+"F9.opPattern","COPY",FACE,{"derivedFrom":subQ12,"instanceName":"1"});Q8=qUnion([makeQuery(id+"F12.opBoolean","SPLIT",EDGE,{"disambiguationData":[topologyDisambiguationEdgeConnected([subQ7,subQ1]),TD([subQ17])],"derivedFrom":subQ15}),makeQuery(id+"F12.opBoolean","SPLIT",EDGE,{"disambiguationData":[topologyDisambiguationEdgeConnected([subQ7,subQ3,subQ5,subQ14]),TD([subQ8])],"derivedFrom":subQ15}),makeQuery(id+"F12.opBoolean","SPLIT",EDGE,{"disambiguationData":[topologyDisambiguationEdgeConnected([subQ7,subQ3,subQ5,subQ14]),TD([subQ16])],"derivedFrom":subQ15}),makeQuery(id+"F12.opBoolean","SPLIT",EDGE,{"disambiguationData":[topologyDisambiguationEdgeConnected([subQ7,subQ1]),TD([subQ11])],"derivedFrom":subQ15}),makeQuery(id+"F12.opBoolean","SPLIT",EDGE,{"disambiguationData":[topologyDisambiguationEdgeConnected([subQ7,subQ1]),TD([subQ8])],"derivedFrom":subQ15}),makeQuery(id+"F12.opBoolean","SPLIT",EDGE,{"disambiguationData":[topologyDisambiguationEdgeConnected([subQ7,subQ3,subQ5,subQ14]),TD([subQ10])],"derivedFrom":subQ15})]);}
            fillet(context, id + "F13", {"entities" : qUnion([Q0, Q1, Q2, Q3, Q4, Q5, Q6, Q7, Q8]), "radius" : 2 * mm, "tangentPropagation" : true, "allowEdgeOverflow" : false});
        }
        {
            var Q0;
            Q0=makeQuery(id+"F11.opPattern","COPY",BODY,{"derivedFrom":makeQuery(id+"F5.opExtrude","SWEPT_BODY",BODY,{"disambiguationData":[OSD([sQuery(id+"F0.wireOp",EDGE,"E0.top"),sQuery(id+"F0.wireOp",EDGE,"E11.top"),sQuery(id+"F0.wireOp",EDGE,"E12.bottom"),sQuery(id+"F0.wireOp",EDGE,"E12.top"),sQuery(id+"F0.wireOp",EDGE,"E12.left"),sQuery(id+"F0.wireOp",EDGE,"E12.right")])]}),"instanceName":"1"});
            var Q1;
            Q1=makeQuery(id+"F3.opRevolve","SWEPT_BODY",BODY,{"disambiguationData":[OSD([sQuery(id+"F0.wireOp",EDGE,"E0.top"),sQuery(id+"F0.wireOp",EDGE,"E0.left"),sQuery(id+"F0.wireOp",EDGE,"E1"),sQuery(id+"F0.wireOp",EDGE,"E4"),sQuery(id+"F0.wireOp",EDGE,"E9.right"),sQuery(id+"F0.wireOp",EDGE,"E11.top"),sQuery(id+"F0.wireOp",EDGE,"E11.left"),sQuery(id+"F0.wireOp",EDGE,"E11.right"),sQuery(id+"F0.wireOp",EDGE,"E12.left"),sQuery(id+"F0.wireOp",EDGE,"E14.right"),sQuery(id+"F0.wireOp",EDGE,"E15.filletArc"),sQuery(id+"F0.wireOp",EDGE,"E17"),sQuery(id+"F0.wireOp",EDGE,"E18"),sQuery(id+"F0.wireOp",EDGE,"E19"),sQuery(id+"F0.wireOp",EDGE,"E20"),sQuery(id+"F0.wireOp",EDGE,"E21.filletArc"),sQuery(id+"F0.wireOp",EDGE,"E22.filletArc"),sQuery(id+"F0.wireOp",EDGE,"E23"),sQuery(id+"F0.wireOp",EDGE,"E24"),sQuery(id+"F0.wireOp",EDGE,"E25"),sQuery(id+"F0.wireOp",EDGE,"E26"),sQuery(id+"F0.wireOp",EDGE,"E28")])]});
            booleanBodies(context, id + "F14", {"operationType" : BooleanOperationType.UNION, "tools" : qUnion([Q0, Q1])});
        }
        {
            var Q0;
            Q0=makeQuery(id+"F11.opPattern","COPY",BODY,{"derivedFrom":makeQuery(id+"F5.opExtrude","SWEPT_BODY",BODY,{"disambiguationData":[OSD([sQuery(id+"F0.wireOp",EDGE,"E0.top"),sQuery(id+"F0.wireOp",EDGE,"E11.top"),sQuery(id+"F0.wireOp",EDGE,"E12.bottom"),sQuery(id+"F0.wireOp",EDGE,"E12.top"),sQuery(id+"F0.wireOp",EDGE,"E12.left"),sQuery(id+"F0.wireOp",EDGE,"E12.right")])]}),"instanceName":"1"});
            var Q1;
            Q1=sQuery(id+"F0.wireOp",EDGE,"E0.left");
            transform(context, id + "F15", {"entities" : qUnion([Q0]), "transformType" : TransformType.TRANSLATION_ENTITY, "oppositeDirectionEntity" : false, "transformLine" : qUnion([Q1]), "makeCopy" : false});
        }
        {
            var Q0;
            Q0=makeQuery(id+"F1.opRevolve","SWEPT_BODY",BODY,{"disambiguationData":[OSD([sQuery(id+"F0.wireOp",EDGE,"E0.bottom"),sQuery(id+"F0.wireOp",EDGE,"E0.top"),sQuery(id+"F0.wireOp",EDGE,"E0.left"),sQuery(id+"F0.wireOp",EDGE,"E0.right"),sQuery(id+"F0.wireOp",EDGE,"E1"),sQuery(id+"F0.wireOp",EDGE,"E7"),sQuery(id+"F0.wireOp",EDGE,"E29")])]});
            var Q1;
            Q1=sQuery(id+"F0.wireOp",EDGE,"E0.left");
            transform(context, id + "F16", {"entities" : qUnion([Q0]), "transformType" : TransformType.TRANSLATION_ENTITY, "oppositeDirectionEntity" : true, "transformLine" : qUnion([Q1]), "makeCopy" : false});
        }
        {
            var Q0;
            {var subQ0=sQuery(id+"F0.wireOp",EDGE,"E0.top");var subQ1=makeQuery(id+"F5.opExtrude","SWEPT_FACE",FACE,{"disambiguationData":[OSD([subQ0,sQuery(id+"F0.wireOp",EDGE,"E12.top")])]});var subQ2=makeQuery(id+"F11.opPattern","COPY",FACE,{"derivedFrom":makeQuery(id+"F10.opBoolean","MERGE",FACE,{"derivedFrom":[subQ1,makeQuery(id+"F9.opPattern","COPY",FACE,{"derivedFrom":subQ1,"instanceName":"1"}),makeQuery(id+"F9.opPattern","COPY",FACE,{"derivedFrom":subQ1,"instanceName":"2"})]}),"instanceName":"1"});var subQ3=sQuery(id+"F0.wireOp",EDGE,"E25");var subQ4=sQuery(id+"F0.wireOp",EDGE,"E19");var subQ5=makeQuery(id+"F3.opRevolve","SWEPT_FACE",FACE,{"disambiguationData":[OSD([subQ4])]});Q0=makeQuery(id+"F14.opBoolean","SPLIT",EDGE,{"disambiguationData":[topologyDisambiguationEdgeConnected([subQ5,subQ2]),TD([makeQuery(id+"F11.opPattern","COPY",FACE,{"derivedFrom":makeQuery(id+"F9.opPattern","COPY",FACE,{"derivedFrom":makeQuery(id+"F5.opExtrude","SWEPT_FACE",FACE,{"disambiguationData":[OSD([sQuery(id+"F0.wireOp",EDGE,"E12.left")])]}),"instanceName":"1"}),"instanceName":"1"})])],"derivedFrom":makeQuery(id+"F3.opRevolve","SWEPT_EDGE",EDGE,{"disambiguationData":[OSD([subQ0,subQ4,subQ3])]})});}
            var Q1;
            {var subQ0=makeQuery(id+"F5.opExtrude","SWEPT_FACE",FACE,{"disambiguationData":[OSD([sQuery(id+"F0.wireOp",EDGE,"E0.top"),sQuery(id+"F0.wireOp",EDGE,"E12.top")])]});Q1=makeQuery(id+"F14.opBoolean","INTERSECT",EDGE,{"disambiguationData":[OD(1.0)],"derivedFrom":[makeQuery(id+"F3.opRevolve","SWEPT_FACE",FACE,{"disambiguationData":[OSD([sQuery(id+"F0.wireOp",EDGE,"E18"),sQuery(id+"F0.wireOp",EDGE,"E24")])]}),makeQuery(id+"F11.opPattern","COPY",FACE,{"derivedFrom":makeQuery(id+"F10.opBoolean","MERGE",FACE,{"derivedFrom":[subQ0,makeQuery(id+"F9.opPattern","COPY",FACE,{"derivedFrom":subQ0,"instanceName":"1"}),makeQuery(id+"F9.opPattern","COPY",FACE,{"derivedFrom":subQ0,"instanceName":"2"})]}),"instanceName":"1"})]});}
            var Q2;
            {var subQ0=makeQuery(id+"F5.opExtrude","SWEPT_FACE",FACE,{"disambiguationData":[OSD([sQuery(id+"F0.wireOp",EDGE,"E0.top"),sQuery(id+"F0.wireOp",EDGE,"E12.top")])]});Q2=makeQuery(id+"F14.opBoolean","INTERSECT",EDGE,{"disambiguationData":[OD(1.0)],"derivedFrom":[makeQuery(id+"F3.opRevolve","SWEPT_FACE",FACE,{"disambiguationData":[OSD([sQuery(id+"F0.wireOp",EDGE,"E17"),sQuery(id+"F0.wireOp",EDGE,"E23")])]}),makeQuery(id+"F11.opPattern","COPY",FACE,{"derivedFrom":makeQuery(id+"F10.opBoolean","MERGE",FACE,{"derivedFrom":[subQ0,makeQuery(id+"F9.opPattern","COPY",FACE,{"derivedFrom":subQ0,"instanceName":"1"}),makeQuery(id+"F9.opPattern","COPY",FACE,{"derivedFrom":subQ0,"instanceName":"2"})]}),"instanceName":"1"})]});}
            var Q3;
            {var subQ0=makeQuery(id+"F5.opExtrude","SWEPT_FACE",FACE,{"disambiguationData":[OSD([sQuery(id+"F0.wireOp",EDGE,"E0.top"),sQuery(id+"F0.wireOp",EDGE,"E12.top")])]});Q3=makeQuery(id+"F14.opBoolean","INTERSECT",EDGE,{"disambiguationData":[OD(2.0)],"derivedFrom":[makeQuery(id+"F3.opRevolve","SWEPT_FACE",FACE,{"disambiguationData":[OSD([sQuery(id+"F0.wireOp",EDGE,"E18"),sQuery(id+"F0.wireOp",EDGE,"E24")])]}),makeQuery(id+"F11.opPattern","COPY",FACE,{"derivedFrom":makeQuery(id+"F10.opBoolean","MERGE",FACE,{"derivedFrom":[subQ0,makeQuery(id+"F9.opPattern","COPY",FACE,{"derivedFrom":subQ0,"instanceName":"1"}),makeQuery(id+"F9.opPattern","COPY",FACE,{"derivedFrom":subQ0,"instanceName":"2"})]}),"instanceName":"1"})]});}
            var Q4;
            {var subQ0=sQuery(id+"F0.wireOp",EDGE,"E0.top");var subQ1=makeQuery(id+"F5.opExtrude","SWEPT_FACE",FACE,{"disambiguationData":[OSD([subQ0,sQuery(id+"F0.wireOp",EDGE,"E12.top")])]});var subQ2=makeQuery(id+"F11.opPattern","COPY",FACE,{"derivedFrom":makeQuery(id+"F10.opBoolean","MERGE",FACE,{"derivedFrom":[subQ1,makeQuery(id+"F9.opPattern","COPY",FACE,{"derivedFrom":subQ1,"instanceName":"1"}),makeQuery(id+"F9.opPattern","COPY",FACE,{"derivedFrom":subQ1,"instanceName":"2"})]}),"instanceName":"1"});var subQ3=sQuery(id+"F0.wireOp",EDGE,"E25");var subQ4=sQuery(id+"F0.wireOp",EDGE,"E19");var subQ5=makeQuery(id+"F3.opRevolve","SWEPT_FACE",FACE,{"disambiguationData":[OSD([subQ4])]});Q4=makeQuery(id+"F14.opBoolean","SPLIT",EDGE,{"disambiguationData":[topologyDisambiguationEdgeConnected([subQ5,subQ2]),TD([makeQuery(id+"F11.opPattern","COPY",FACE,{"derivedFrom":makeQuery(id+"F5.opExtrude","SWEPT_FACE",FACE,{"disambiguationData":[OSD([sQuery(id+"F0.wireOp",EDGE,"E12.left")])]}),"instanceName":"1"})])],"derivedFrom":makeQuery(id+"F3.opRevolve","SWEPT_EDGE",EDGE,{"disambiguationData":[OSD([subQ0,subQ4,subQ3])]})});}
            var Q5;
            {var subQ0=makeQuery(id+"F5.opExtrude","SWEPT_FACE",FACE,{"disambiguationData":[OSD([sQuery(id+"F0.wireOp",EDGE,"E0.top"),sQuery(id+"F0.wireOp",EDGE,"E12.top")])]});Q5=makeQuery(id+"F14.opBoolean","INTERSECT",EDGE,{"disambiguationData":[OD(0.0)],"derivedFrom":[makeQuery(id+"F3.opRevolve","SWEPT_FACE",FACE,{"disambiguationData":[OSD([sQuery(id+"F0.wireOp",EDGE,"E17"),sQuery(id+"F0.wireOp",EDGE,"E23")])]}),makeQuery(id+"F11.opPattern","COPY",FACE,{"derivedFrom":makeQuery(id+"F10.opBoolean","MERGE",FACE,{"derivedFrom":[subQ0,makeQuery(id+"F9.opPattern","COPY",FACE,{"derivedFrom":subQ0,"instanceName":"1"}),makeQuery(id+"F9.opPattern","COPY",FACE,{"derivedFrom":subQ0,"instanceName":"2"})]}),"instanceName":"1"})]});}
            var Q6;
            {var subQ0=makeQuery(id+"F5.opExtrude","SWEPT_FACE",FACE,{"disambiguationData":[OSD([sQuery(id+"F0.wireOp",EDGE,"E0.top"),sQuery(id+"F0.wireOp",EDGE,"E12.top")])]});Q6=makeQuery(id+"F14.opBoolean","INTERSECT",EDGE,{"disambiguationData":[OD(0.0)],"derivedFrom":[makeQuery(id+"F3.opRevolve","SWEPT_FACE",FACE,{"disambiguationData":[OSD([sQuery(id+"F0.wireOp",EDGE,"E18"),sQuery(id+"F0.wireOp",EDGE,"E24")])]}),makeQuery(id+"F11.opPattern","COPY",FACE,{"derivedFrom":makeQuery(id+"F10.opBoolean","MERGE",FACE,{"derivedFrom":[subQ0,makeQuery(id+"F9.opPattern","COPY",FACE,{"derivedFrom":subQ0,"instanceName":"1"}),makeQuery(id+"F9.opPattern","COPY",FACE,{"derivedFrom":subQ0,"instanceName":"2"})]}),"instanceName":"1"})]});}
            var Q7;
            {var subQ0=sQuery(id+"F0.wireOp",EDGE,"E0.top");var subQ1=makeQuery(id+"F5.opExtrude","SWEPT_FACE",FACE,{"disambiguationData":[OSD([subQ0,sQuery(id+"F0.wireOp",EDGE,"E12.top")])]});var subQ2=makeQuery(id+"F11.opPattern","COPY",FACE,{"derivedFrom":makeQuery(id+"F10.opBoolean","MERGE",FACE,{"derivedFrom":[subQ1,makeQuery(id+"F9.opPattern","COPY",FACE,{"derivedFrom":subQ1,"instanceName":"1"}),makeQuery(id+"F9.opPattern","COPY",FACE,{"derivedFrom":subQ1,"instanceName":"2"})]}),"instanceName":"1"});var subQ3=sQuery(id+"F0.wireOp",EDGE,"E25");var subQ4=sQuery(id+"F0.wireOp",EDGE,"E19");var subQ5=makeQuery(id+"F3.opRevolve","SWEPT_FACE",FACE,{"disambiguationData":[OSD([subQ4])]});Q7=makeQuery(id+"F14.opBoolean","SPLIT",EDGE,{"disambiguationData":[topologyDisambiguationEdgeConnected([subQ5,subQ2]),TD([makeQuery(id+"F11.opPattern","COPY",FACE,{"derivedFrom":makeQuery(id+"F9.opPattern","COPY",FACE,{"derivedFrom":makeQuery(id+"F5.opExtrude","SWEPT_FACE",FACE,{"disambiguationData":[OSD([sQuery(id+"F0.wireOp",EDGE,"E12.left")])]}),"instanceName":"2"}),"instanceName":"1"})])],"derivedFrom":makeQuery(id+"F3.opRevolve","SWEPT_EDGE",EDGE,{"disambiguationData":[OSD([subQ0,subQ4,subQ3])]})});}
            var Q8;
            {var subQ0=makeQuery(id+"F5.opExtrude","SWEPT_FACE",FACE,{"disambiguationData":[OSD([sQuery(id+"F0.wireOp",EDGE,"E0.top"),sQuery(id+"F0.wireOp",EDGE,"E12.top")])]});Q8=makeQuery(id+"F14.opBoolean","INTERSECT",EDGE,{"disambiguationData":[OD(2.0)],"derivedFrom":[makeQuery(id+"F3.opRevolve","SWEPT_FACE",FACE,{"disambiguationData":[OSD([sQuery(id+"F0.wireOp",EDGE,"E17"),sQuery(id+"F0.wireOp",EDGE,"E23")])]}),makeQuery(id+"F11.opPattern","COPY",FACE,{"derivedFrom":makeQuery(id+"F10.opBoolean","MERGE",FACE,{"derivedFrom":[subQ0,makeQuery(id+"F9.opPattern","COPY",FACE,{"derivedFrom":subQ0,"instanceName":"1"}),makeQuery(id+"F9.opPattern","COPY",FACE,{"derivedFrom":subQ0,"instanceName":"2"})]}),"instanceName":"1"})]});}
            fillet(context, id + "F17", {"entities" : qUnion([Q0, Q1, Q2, Q3, Q4, Q5, Q6, Q7, Q8]), "radius" : 2 * mm, "tangentPropagation" : true, "allowEdgeOverflow" : false});
        }
        {
            var Q0;
            Q0=makeQuery(id+"F3.opRevolve","SWEPT_EDGE",EDGE,{"disambiguationData":[OSD([sQuery(id+"F0.wireOp",EDGE,"E0.top"),sQuery(id+"F0.wireOp",EDGE,"E26")])]});
            fillet(context, id + "F18", {"entities" : qUnion([Q0]), "radius" : 2 * mm, "tangentPropagation" : true, "allowEdgeOverflow" : false});
        }
    });
